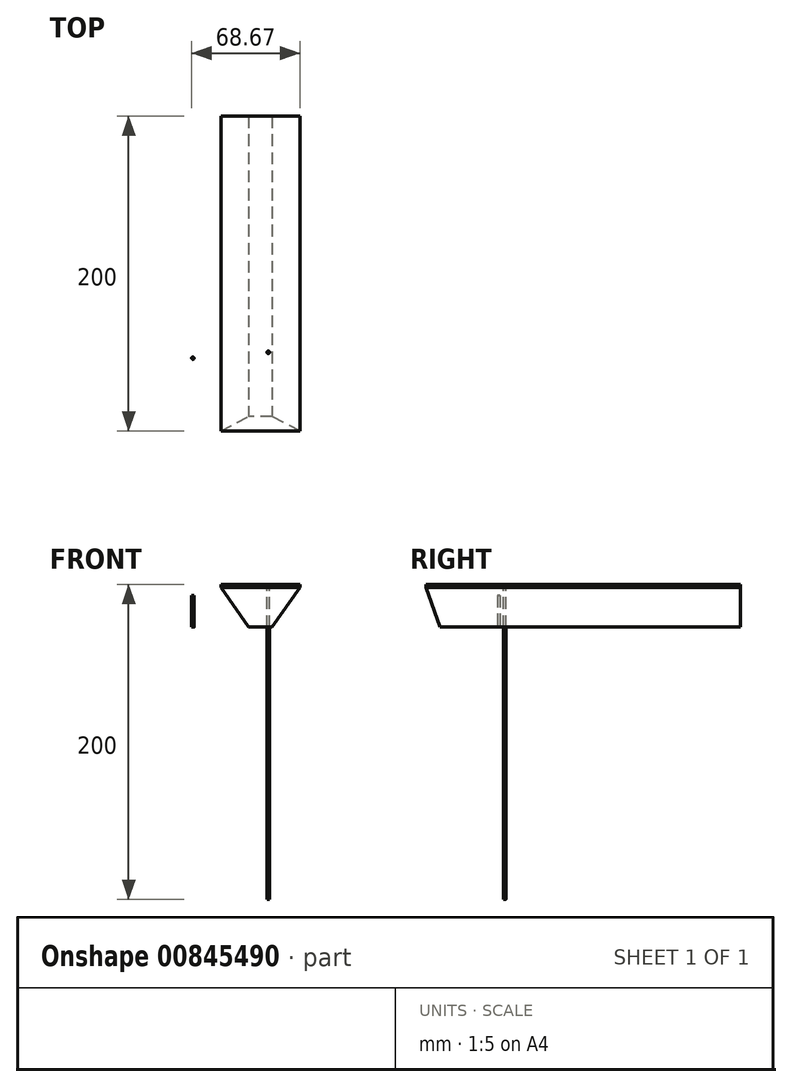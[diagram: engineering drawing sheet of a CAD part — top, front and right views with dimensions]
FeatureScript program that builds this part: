
annotation { "Feature Type Name" : "Feature", "Feature Type Description" : "" }
export const myFeature = defineFeature(function(context is Context, id is Id, definition is map)
    precondition{}
    {
        {
            var Q0;
            Q0=qCreatedBy(makeId("Top.planeOp"),FACE);
            var sketch = newSketch(context, id + "F0", { "sketchPlane" : qUnion([Q0])});
            skLineSegment(sketch, "E0.bottom", {"start": v(0, 0) * mm, "end": v(50, 0) * mm});
            skLineSegment(sketch, "E0.top", {"start": v(0, 200) * mm, "end": v(50, 200) * mm});
            skLineSegment(sketch, "E0.left", {"start": v(0, 0) * mm, "end": v(0, 200) * mm});
            skLineSegment(sketch, "E0.right", {"start": v(50, 0) * mm, "end": v(50, 200) * mm});
            skSolve(sketch);
        }
        {
            var Q0;
            Q0=qSketchRegion(id+"F0",true);
            extrude(context, id + "F1", {"entities" : qUnion([Q0]), "offsetDistance" : 25 * mm, "depth" : 25 * mm});
        }
        {
            var Q0;
            Q0=makeQuery(id+"F1.opExtrude","SWEPT_FACE",FACE,{"disambiguationData":[OSD([sQuery(id+"F0.wireOp",EDGE,"E0.bottom")])]});
            var sketch = newSketch(context, id + "F2", { "sketchPlane" : qUnion([Q0])});
            skLineSegment(sketch, "E1", {"start": v(0, 25) * mm, "end": v(17.5, 0) * mm});
            skLineSegment(sketch, "E2", {"start": v(17.5, 0) * mm, "end": v(0, 0) * mm});
            skLineSegment(sketch, "E3", {"start": v(0, 0) * mm, "end": v(0, 25) * mm});
            skLineSegment(sketch, "E4", {"start": v(32.5, 0) * mm, "end": v(50, 0) * mm});
            skLineSegment(sketch, "E5", {"start": v(50, 0) * mm, "end": v(50, 25) * mm});
            skLineSegment(sketch, "E6", {"start": v(50, 25) * mm, "end": v(32.5, 0) * mm});
            skSolve(sketch);
        }
        {
            var Q0;
            Q0=qSketchRegion(id+"F2",true);
            extrude(context, id + "F3", {"entities" : qUnion([Q0]), "operationType" : NewBodyOperationType.REMOVE, "endBound" : BoundingType.THROUGH_ALL, "oppositeDirection" : true, "depth" : 25 * mm});
        }
        {
            var Q0;
            Q0=qCreatedBy(makeId("Right.planeOp"),FACE);
            var sketch = newSketch(context, id + "F4", { "sketchPlane" : qUnion([Q0])});
            skLineSegment(sketch, "E7", {"start": v(0, 0) * mm, "end": v(0, 25) * mm});
            skLineSegment(sketch, "E8", {"start": v(0, 25) * mm, "end": v(9.1, 0) * mm});
            skLineSegment(sketch, "E9", {"start": v(9.1, 0) * mm, "end": v(0, 0) * mm});
            skSolve(sketch);
        }
        {
            var Q0;
            Q0=qSketchRegion(id+"F4",true);
            extrude(context, id + "F5", {"entities" : qUnion([Q0]), "operationType" : NewBodyOperationType.REMOVE, "endBound" : BoundingType.THROUGH_ALL, "depth" : 25 * mm});
        }
        {
            var Q0;
            Q0=makeQuery(id+"F1.opExtrude","CAP_FACE",FACE,{"disambiguationData":[OSD([sQuery(id+"F0.wireOp",EDGE,"E0.bottom"),sQuery(id+"F0.wireOp",EDGE,"E0.top"),sQuery(id+"F0.wireOp",EDGE,"E0.left"),sQuery(id+"F0.wireOp",EDGE,"E0.right")])],"isStart":false});
            var sketch = newSketch(context, id + "F6", { "sketchPlane" : qUnion([Q0])});
            skLineSegment(sketch, "E10.bottom", {"start": v(0, 0) * mm, "end": v(50, 0) * mm});
            skLineSegment(sketch, "E10.top", {"start": v(0, 200) * mm, "end": v(50, 200) * mm});
            skLineSegment(sketch, "E10.left", {"start": v(0, 0) * mm, "end": v(0, 200) * mm});
            skLineSegment(sketch, "E10.right", {"start": v(50, 0) * mm, "end": v(50, 200) * mm});
            skSolve(sketch);
        }
        {
            var Q0;
            Q0=qSketchRegion(id+"F6",true);
            extrude(context, id + "F7", {"entities" : qUnion([Q0]), "depth" : 2 * mm});
        }
        {
            var Q0;
            Q0=makeQuery(id+"F7.opExtrude","CAP_FACE",FACE,{"disambiguationData":[OSD([sQuery(id+"F6.wireOp",EDGE,"E10.bottom"),sQuery(id+"F6.wireOp",EDGE,"E10.top"),sQuery(id+"F6.wireOp",EDGE,"E10.left"),sQuery(id+"F6.wireOp",EDGE,"E10.right")])],"isStart":false});
            var sketch = newSketch(context, id + "F8", { "sketchPlane" : qUnion([Q0])});
            skCircle(sketch, "E11", {"center": v(30, 50) * mm, "radius": 0.8 * mm});
            skSolve(sketch);
        }
        {
            var Q0;
            Q0=qSketchRegion(id+"F8",true);
            extrude(context, id + "F9", {"entities" : qUnion([Q0]), "oppositeDirection" : true, "depth" : 200 * mm});
        }
        {
            var Q0;
            Q0=qCreatedBy(makeId("Top.planeOp"),FACE);
            var sketch = newSketch(context, id + "F10", { "sketchPlane" : qUnion([Q0])});
            skCircle(sketch, "E12", {"center": v(-17.92, 46.27) * mm, "radius": 0.75 * mm});
            skSolve(sketch);
        }
        {
            var Q0;
            Q0=qSketchRegion(id+"F10",true);
            extrude(context, id + "F11", {"entities" : qUnion([Q0]), "depth" : 20 * mm});
        }
    });
